# Revit family: Vent_Cap-Navien-Outdoor-Kit-NPE-2
name_source: partatom
category: Mechanical Equipment
units: mm (PartAtom-declared; Revit-internal decimal feet)

## family parameters
Cut with Voids When Loaded = No
Host = Face
OmniClass Number = 23.65.35.11
OmniClass Title = Supply Water Heaters
Part Type = Normal
Room Calculation Point = No
Round Connector Dimension = Use Diameter
Shared = No

## types (1)
- Outdoor Vent Kit for NPE-2 Series
    Assembly Code = D
    Default Elevation = 48 "
    Depth = 13.1 "
    Description = Designed for use with NPE-2 series units when installing your unit outside. Required for outdoor installations.

1 year warranty from date of purchase.
    Finish = Polypropylene - Navien - White
    Height = 7.5 "
    Installation Type = Outdoor Vent Cover - Wall Mounted
    Keynote = Division 22
    Manufacturer = Navien, Inc.
    Manufacturer Fax Number = (949) 420-0430
    Model = 30025801A
    Product Documentation Link = https://www.navieninc.com
    Product Name = Outdoor Vent Kit for NPE-2 Series
    Product Page URL = https://www.navieninc.com
    URL = https://www.navieninc.com
    Version = 2019 - v1.0.a
    Warranty = https://www.navieninc.com
    Weight = 0.00 lbf
    Width = 17.8 "

## geometry (parser evidence)
native form markers: Sweep x3
no freeform markers — native parametric forms only
